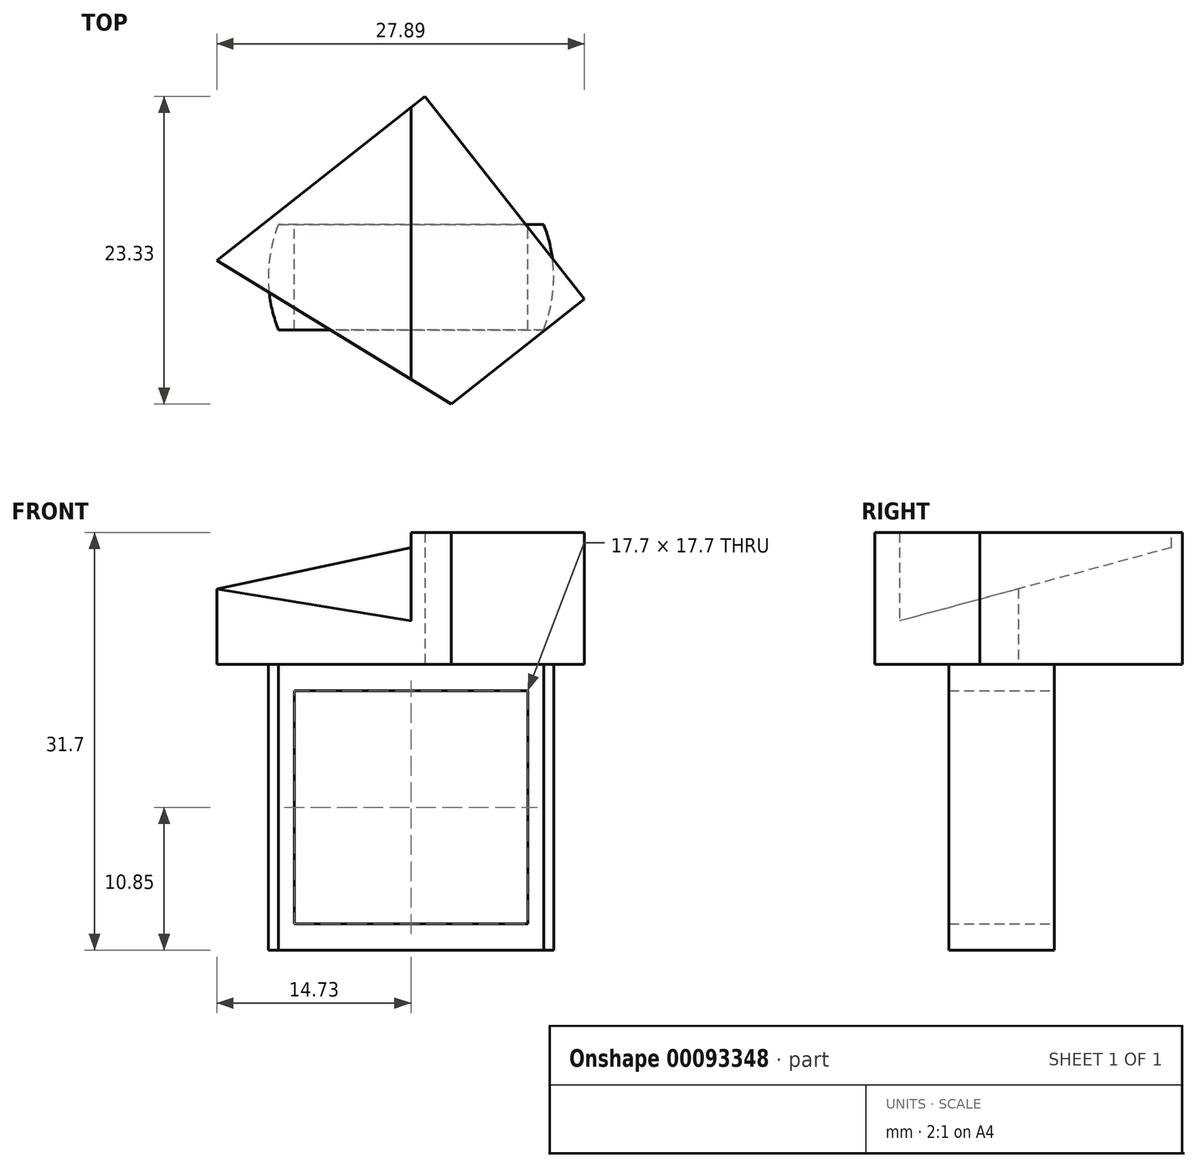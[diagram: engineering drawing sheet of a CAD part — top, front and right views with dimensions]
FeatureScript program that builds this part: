
annotation { "Feature Type Name" : "Feature", "Feature Type Description" : "" }
export const myFeature = defineFeature(function(context is Context, id is Id, definition is map)
    precondition{}
    {
        {
            var Q0;
            Q0=qCreatedBy(makeId("Front.planeOp"),FACE);
            var sketch = newSketch(context, id + "F0", { "sketchPlane" : qUnion([Q0])});
            skCircle(sketch, "E0", {"center": v(0, 0) * mm, "radius": 8.85 * mm});
            skLineSegment(sketch, "E1", {"start": v(0, 8.85) * mm, "end": v(8.85, 0) * mm});
            skLineSegment(sketch, "E2", {"start": v(8.85, 0) * mm, "end": v(8.85, 8.85) * mm});
            skLineSegment(sketch, "E3", {"start": v(8.85, 8.85) * mm, "end": v(0, 8.85) * mm});
            skLineSegment(sketch, "E4.MirrorCS", {"start": v(8.85, -8.85) * mm, "end": v(0, -8.85) * mm});
            skLineSegment(sketch, "E5.MirrorCS", {"start": v(8.85, 0) * mm, "end": v(8.85, -8.85) * mm});
            skLineSegment(sketch, "E6.MirrorCS", {"start": v(-8.85, 8.85) * mm, "end": v(0, 8.85) * mm});
            skLineSegment(sketch, "E7.MirrorCS", {"start": v(-8.85, 0) * mm, "end": v(-8.85, 8.85) * mm});
            skLineSegment(sketch, "E8.MirrorCS", {"start": v(-8.85, -8.85) * mm, "end": v(0, -8.85) * mm});
            skLineSegment(sketch, "E9.MirrorCS", {"start": v(-8.85, 0) * mm, "end": v(-8.85, -8.85) * mm});
            skLineSegment(sketch, "E10.0", {"start": v(-10.85, 0) * mm, "end": v(-10.85, 10.85) * mm});
            skLineSegment(sketch, "E10.1", {"start": v(-10.85, 0) * mm, "end": v(-10.85, -10.85) * mm});
            skLineSegment(sketch, "E10.2", {"start": v(-10.85, 10.85) * mm, "end": v(0, 10.85) * mm});
            skLineSegment(sketch, "E10.3", {"start": v(-10.85, -10.85) * mm, "end": v(0, -10.85) * mm});
            skLineSegment(sketch, "E10.4", {"start": v(10.85, 10.85) * mm, "end": v(0, 10.85) * mm});
            skLineSegment(sketch, "E10.5", {"start": v(10.85, 0) * mm, "end": v(10.85, 10.85) * mm});
            skLineSegment(sketch, "E10.6", {"start": v(10.85, 0) * mm, "end": v(10.85, -10.85) * mm});
            skLineSegment(sketch, "E10.7", {"start": v(10.85, -10.85) * mm, "end": v(0, -10.85) * mm});
            skSolve(sketch);
        }
        {
            var Q0;
            Q0=makeQuery(id+"F0.imprint","IMPRINT",FACE,{"disambiguationData":[TD([[makeQuery(id+"F0.imprint","IMPRINT",EDGE,{"derivedFrom":sQuery(id+"F0.wireOp",EDGE,"E2")}),-1.0]])]});
            extrude(context, id + "F1", {"entities" : qUnion([Q0]), "depth" : 4 * mm, "hasSecondDirection" : true, "secondDirectionOppositeDirection" : true, "secondDirectionDepth" : 4 * mm});
        }
        {
            var Q0;
            Q0=makeQuery(id+"F1.opExtrude","SWEPT_FACE",FACE,{"disambiguationData":[OSD([sQuery(id+"F0.wireOp",EDGE,"E10.2"),sQuery(id+"F0.wireOp",EDGE,"E10.4")])]});
            var sketch = newSketch(context, id + "F2", { "sketchPlane" : qUnion([Q0])});
            skLineSegment(sketch, "E11", {"start": v(3.05, -9.63) * mm, "end": v(13.16, -1.65) * mm});
            skLineSegment(sketch, "E12", {"start": v(13.16, -1.65) * mm, "end": v(1.05, 13.7) * mm});
            skLineSegment(sketch, "E13", {"start": v(1.05, 13.7) * mm, "end": v(-14.73, 1.25) * mm});
            skLineSegment(sketch, "E14", {"start": v(-14.73, 1.25) * mm, "end": v(3.05, -9.63) * mm});
            skSolve(sketch);
        }
        {
            var Q0;
            {var subQ0=sQuery(id+"F2.wireOp",EDGE,"E13");var subQ1=sQuery(id+"F2.wireOp",EDGE,"E12");var subQ2=makeQuery(id+"F2.imprint","INTERSECT",VERTEX,{"derivedFrom":[subQ1,subQ0]});Q0=makeQuery(id+"F2.imprint","IMPRINT",FACE,{"disambiguationData":[TD([[makeQuery(id+"F2.imprint","IMPRINT",EDGE,{"disambiguationData":[TD([[subQ2,1.0]])],"derivedFrom":subQ1}),1.0]])]});}
            var Q1;
            {var subQ1=sQuery(id+"F0.wireOp",EDGE,"E10.4");var subQ2=sQuery(id+"F0.wireOp",EDGE,"E10.2");var subQ7=sQuery(id+"F2.wireOp",EDGE,"E11");var subQ8=makeQuery(id+"F1.opExtrude","CAP_EDGE",EDGE,{"disambiguationData":[OSD([subQ2,subQ1])],"isStart":false});var subQ9=makeQuery(id+"F2.imprint","INTERSECT",VERTEX,{"derivedFrom":[subQ8,subQ7]});Q1=makeQuery(id+"F2.imprint","IMPRINT",FACE,{"disambiguationData":[TD([[makeQuery(id+"F2.imprint","IMPRINT",EDGE,{"disambiguationData":[TD([[subQ9,-1.0]])],"derivedFrom":subQ7}),1.0]])]});}
            var Q2;
            {var subQ0=sQuery(id+"F2.wireOp",EDGE,"E14");var subQ1=sQuery(id+"F2.wireOp",EDGE,"E13");var subQ2=makeQuery(id+"F2.imprint","INTERSECT",VERTEX,{"derivedFrom":[subQ1,subQ0]});Q2=makeQuery(id+"F2.imprint","IMPRINT",FACE,{"disambiguationData":[TD([[makeQuery(id+"F2.imprint","IMPRINT",EDGE,{"disambiguationData":[TD([[subQ2,1.0]])],"derivedFrom":subQ1}),1.0]])]});}
            var Q3;
            {var subQ0=sQuery(id+"F2.wireOp",EDGE,"E14");var subQ1=sQuery(id+"F2.wireOp",EDGE,"E11");var subQ2=makeQuery(id+"F2.imprint","INTERSECT",VERTEX,{"derivedFrom":[subQ1,subQ0]});Q3=makeQuery(id+"F2.imprint","IMPRINT",FACE,{"disambiguationData":[TD([[makeQuery(id+"F2.imprint","IMPRINT",EDGE,{"disambiguationData":[TD([[subQ2,-1.0]])],"derivedFrom":subQ1}),1.0]])]});}
            var Q4;
            {var subQ0=sQuery(id+"F2.wireOp",EDGE,"E12");var subQ1=sQuery(id+"F2.wireOp",EDGE,"E11");var subQ2=makeQuery(id+"F2.imprint","INTERSECT",VERTEX,{"derivedFrom":[subQ1,subQ0]});Q4=makeQuery(id+"F2.imprint","IMPRINT",FACE,{"disambiguationData":[TD([[makeQuery(id+"F2.imprint","IMPRINT",EDGE,{"disambiguationData":[TD([[subQ2,1.0]])],"derivedFrom":subQ1}),1.0]])]});}
            extrude(context, id + "F3", {"entities" : qUnion([Q0, Q1, Q2, Q3, Q4]), "operationType" : NewBodyOperationType.ADD, "depth" : 10 * mm});
        }
        {
            var Q0;
            Q0=qCreatedBy(makeId("Right.planeOp"),FACE);
            var sketch = newSketch(context, id + "F4", { "sketchPlane" : qUnion([Q0])});
            skLineSegment(sketch, "E15", {"start": v(17.97, 21.09) * mm, "end": v(-36.7, 6.32) * mm});
            skLineSegment(sketch, "E16", {"start": v(-36.7, 6.32) * mm, "end": v(-36.7, 33.67) * mm});
            skLineSegment(sketch, "E17", {"start": v(-36.7, 33.67) * mm, "end": v(17.97, 21.09) * mm});
            skSolve(sketch);
        }
        {
            var Q0;
            Q0=makeQuery(id+"F4.imprint","IMPRINT",FACE,{"disambiguationData":[TD([[makeQuery(id+"F4.imprint","IMPRINT",EDGE,{"derivedFrom":sQuery(id+"F4.wireOp",EDGE,"E15")}),-1.0]])]});
            extrude(context, id + "F5", {"entities" : qUnion([Q0]), "operationType" : NewBodyOperationType.REMOVE, "oppositeDirection" : true, "depth" : 25 * mm});
        }
        {
            var Q0;
            Q0=makeQuery(id+"F1.opExtrude","SWEPT_FACE",FACE,{"disambiguationData":[OSD([sQuery(id+"F0.wireOp",EDGE,"E10.3"),sQuery(id+"F0.wireOp",EDGE,"E10.7")])]});
            var sketch = newSketch(context, id + "F6", { "sketchPlane" : qUnion([Q0])});
            skCircle(sketch, "E18", {"center": v(0, 0) * mm, "radius": 10.82 * mm});
            skLineSegment(sketch, "E19", {"start": v(9.7, 4.81) * mm, "end": v(13.92, 4.81) * mm});
            skLineSegment(sketch, "E20", {"start": v(13.92, 4.81) * mm, "end": v(13.92, -5.04) * mm});
            skLineSegment(sketch, "E21", {"start": v(13.92, -5.04) * mm, "end": v(9.58, -5.04) * mm});
            skLineSegment(sketch, "E22.MirrorCS", {"start": v(-9.7, 4.81) * mm, "end": v(-13.92, 4.81) * mm});
            skLineSegment(sketch, "E23.MirrorCS", {"start": v(-13.92, 4.81) * mm, "end": v(-13.92, -5.04) * mm});
            skLineSegment(sketch, "E24.MirrorCS", {"start": v(-13.92, -5.04) * mm, "end": v(-9.58, -5.04) * mm});
            skSolve(sketch);
        }
        {
            var Q0;
            {var subQ1=sQuery(id+"F0.wireOp",EDGE,"E10.7");var subQ7=makeQuery(id+"F1.opExtrude","SWEPT_EDGE",EDGE,{"disambiguationData":[OSD([sQuery(id+"F0.wireOp",EDGE,"E10.6"),subQ1])]});Q0=makeQuery(id+"F6.imprint","IMPRINT",FACE,{"disambiguationData":[TD([[makeQuery(id+"F6.imprint","IMPRINT",EDGE,{"derivedFrom":subQ7}),-1.0]])]});}
            var Q1;
            {var subQ2=sQuery(id+"F0.wireOp",EDGE,"E10.3");var subQ7=makeQuery(id+"F1.opExtrude","SWEPT_EDGE",EDGE,{"disambiguationData":[OSD([sQuery(id+"F0.wireOp",EDGE,"E10.1"),subQ2])]});Q1=makeQuery(id+"F6.imprint","IMPRINT",FACE,{"disambiguationData":[TD([[makeQuery(id+"F6.imprint","IMPRINT",EDGE,{"derivedFrom":subQ7}),1.0]])]});}
            var Q2;
            {var subQ0=sQuery(id+"F2.wireOp",EDGE,"E13");var subQ1=sQuery(id+"F2.wireOp",EDGE,"E14");Q2=makeQuery(id+"F3.boolean.opBoolean","SPLIT",FACE,{"disambiguationData":[TD([makeQuery(id+"F1.opExtrude","SWEPT_FACE",FACE,{"disambiguationData":[OSD([sQuery(id+"F0.wireOp",EDGE,"E10.0"),sQuery(id+"F0.wireOp",EDGE,"E10.1")])]})])],"derivedFrom":makeQuery(id+"F3.opExtrude","CAP_FACE",FACE,{"disambiguationData":[OSD([sQuery(id+"F2.wireOp",EDGE,"E11"),sQuery(id+"F2.wireOp",EDGE,"E12"),subQ0,subQ1])],"isStart":true})});}
            extrude(context, id + "F7", {"entities" : qUnion([Q0, Q1]), "operationType" : NewBodyOperationType.REMOVE, "oppositeDirection" : true, "endBoundEntityFace" : qUnion([Q2]), "depth" : 21.7 * mm});
        }
    });
